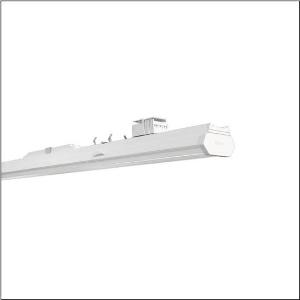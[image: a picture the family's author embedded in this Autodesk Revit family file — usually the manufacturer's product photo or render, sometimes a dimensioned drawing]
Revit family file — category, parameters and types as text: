
# Revit family: licross_r__11_protected_mo_51td11dn495g_7274
name_source: partatom
category: Lighting Fixtures
units: mm (PartAtom-declared; Revit-internal decimal feet)

## family parameters
Cut with Voids When Loaded = No
Host = Face
Light Source = No
Part Type = Normal
Room Calculation Point = No
Round Connector Dimension = Use Diameter
Shared = No

## types (1)
- --- (1 x LED, 9930 lm, 57.1 W, 4000K)
    Apparent Load = 57 VA
    CIE Flux Codes = 83 94 98 100 100
    Color Rendering = 80
    Color Temperature = 4000K
    Default Elevation = 1800 mm
    Description = Licross® 11 Protected MO, luminaire insert, of sheet steel, galvanised, coil coated, white, length: 1.500mm, width: 90mm, height: 101mm, LED rated luminous flux: 9.930lm, light colour: 840, control gear: DALI 2, with plug, 5-pole, with phase selection, mains connection: 220..240V, AC, 50/60Hz, rated input power: 57W, halogen-free wiring, primary light control with lens, of plastic, primary optical cover: cover, of PMMA, light emission: direct distribution, primary light characteristic: symmetric, protection rating (complete): IP54, insulation class (complete): insulation class I (protective earthing), certification: CE, ENEC, VDE, UKCA, protection symbol: D if used in an environment with non-conductive dust loads with corresponding accessories, impact resistance: IK06, permissible ambient temperature for indoor applications: -25..+35°C, corresponds to IFS (International Featured Standards) requirements for safety and quality in the food industry, reducing of maximum allowable ambient temperature of 5°C with ceiling mounting, LABS conformity tested according to VDMA 24364:2018-05, packaging unit: 1 piece
    Height = 92 mm
    Lamp = 1 x LED
    Lamp Light Flux = 9930 lm
    Lamp Power = 57.1 W
    Lamp count = 1
    Length = 1500 mm
    Luminous efficacy = 174 lm/W
    Manufacturer = Siteco
    ModVariant = No
    Model = 51TD11DN495G
    Mounting Place = Ceiling
    Mounting Type = Pendant
    Number of Poles = 1
    OnlyDefault = Yes
    Power Factor = 1
    Product Name = Licross® 11 Protected MO
    Product group = luminaire insert
    ProductGroupID = 901
    Protection Class = Protection class I
    Protection Degree = IP 54
    RLX_Detail_Level = 1
    RLX_Emergency_Light_Flux = 0 lm
    RLX_Emergency_Type = 0
    RLX_Emergency_Type_DB = No
    RlxData = <blob elided: 24153 chars, md5=fd82de7b>
    Socket = socket
    Standby Power = 0 W
    System Light Flux = 9930 lm
    System Power = 57 W
    Type Comments = factory setting: luminous flux: 100 % | dim-lin: 254 | 378 mA
    Type Image = l_1256145.jpg
    URL = http://relux.com
    VarID = @adj_069861
    Voltage = 0 V
    Weight = 0.00 kg
    Width = 88 mm

## geometry (parser evidence)
native form markers: Blend x4, Sweep x12
no freeform markers — native parametric forms only
